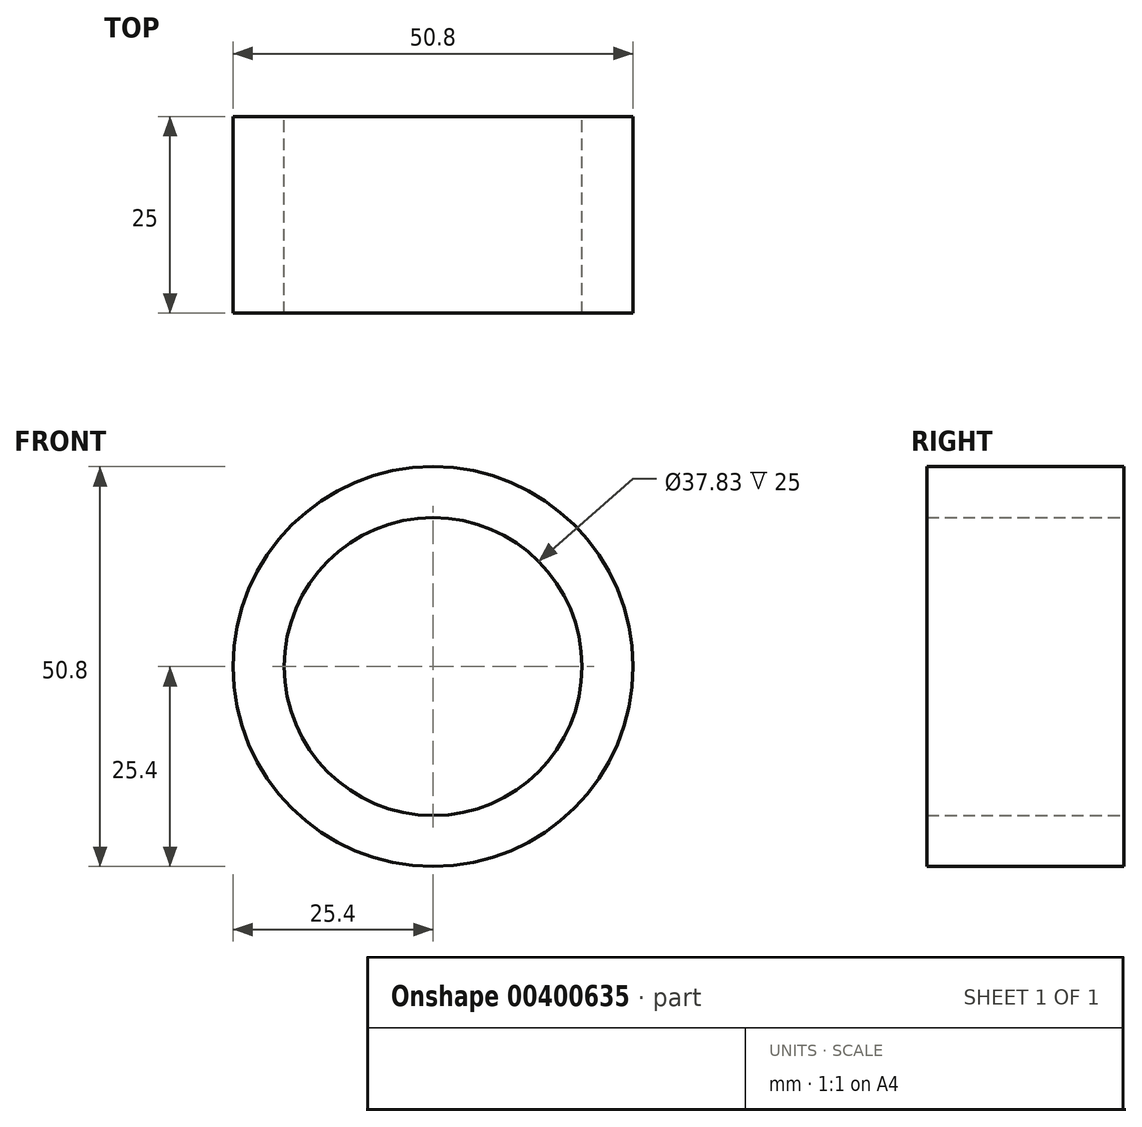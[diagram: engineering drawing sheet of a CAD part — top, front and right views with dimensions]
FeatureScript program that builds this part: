
annotation { "Feature Type Name" : "Feature", "Feature Type Description" : "" }
export const myFeature = defineFeature(function(context is Context, id is Id, definition is map)
    precondition{}
    {
        {
            var Q0;
            Q0=qCreatedBy(makeId("Front.planeOp"),FACE);
            var sketch = newSketch(context, id + "F0", { "sketchPlane" : qUnion([Q0])});
            skCircle(sketch, "E0", {"center": v(0, 0) * mm, "radius": 25.4 * mm});
            skSolve(sketch);
        }
        {
            var Q0;
            Q0 = qSketchRegion(id + "F0", true);
            extrude(context, id + "F1", {"entities" : qUnion([Q0]), "depth" : 25 * mm, "symmetric" : true});
        }
        {
            var Q0;
            Q0=makeQuery(id+"F1.opExtrude","CAP_FACE",FACE,{"disambiguationData":[OSD([sQuery(id+"F0.wireOp",EDGE,"E0")])],"isStart":false});
            var sketch = newSketch(context, id + "F2", { "sketchPlane" : qUnion([Q0])});
            skCircle(sketch, "E1", {"center": v(0, 0) * mm, "radius": 18.91 * mm});
            skSolve(sketch);
        }
        {
            var Q0;
            Q0 = qSketchRegion(id + "F2", true);
            extrude(context, id + "F3", {"entities" : qUnion([Q0]), "operationType" : NewBodyOperationType.REMOVE, "depth" : 50 * mm, "symmetric" : true});
        }
    });
